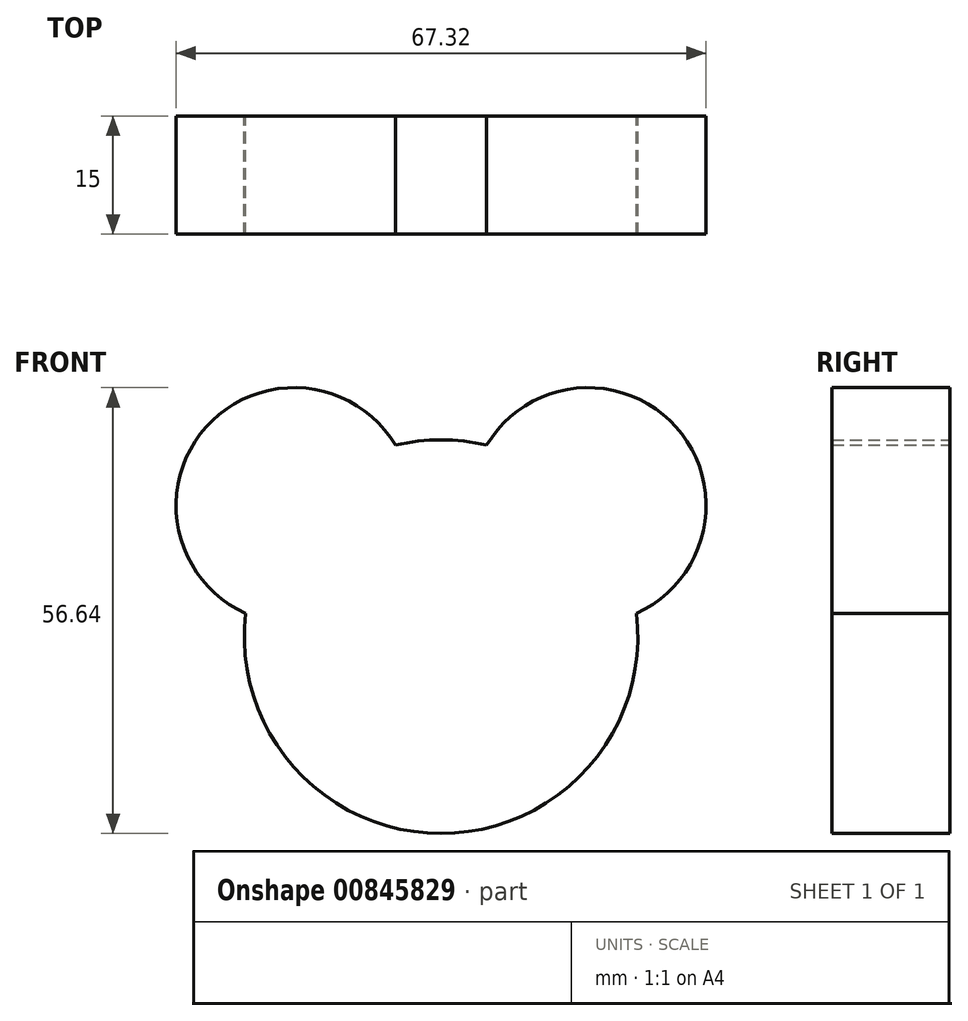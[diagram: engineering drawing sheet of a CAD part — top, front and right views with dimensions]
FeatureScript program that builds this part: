
annotation { "Feature Type Name" : "Feature", "Feature Type Description" : "" }
export const myFeature = defineFeature(function(context is Context, id is Id, definition is map)
    precondition{}
    {
        {
            var Q0;
            Q0=qCreatedBy(makeId("Front.planeOp"),FACE);
            var sketch = newSketch(context, id + "F0", { "sketchPlane" : qUnion([Q0])});
            skArc(sketch, "E0", {"start": v(-24.82, 2.96) * mm, "mid": v(0, -25) * mm, "end": v(24.82, 2.96) * mm});
            skArc(sketch, "E1", {"start": v(-5.78, 24.32) * mm, "mid": v(-29.86, 26.62) * mm, "end": v(-24.82, 2.96) * mm});
            skArc(sketch, "E2", {"start": v(24.82, 2.96) * mm, "mid": v(29.86, 26.62) * mm, "end": v(5.78, 24.32) * mm});
            skArc(sketch, "E3.trimOffspring", {"start": v(5.78, 24.32) * mm, "mid": v(0, 25) * mm, "end": v(-5.78, 24.32) * mm});
            skSolve(sketch);
        }
        {
            var Q0;
            Q0=makeQuery(id+"F0.imprint","IMPRINT",FACE,{"disambiguationData":[TD([[makeQuery(id+"F0.imprint","IMPRINT",EDGE,{"derivedFrom":sQuery(id+"F0.wireOp",EDGE,"E0")}),1.0]])]});
            extrude(context, id + "F1", {"entities" : qUnion([Q0]), "depth" : 15 * mm, "offsetDistance" : 25 * mm});
        }
    });
